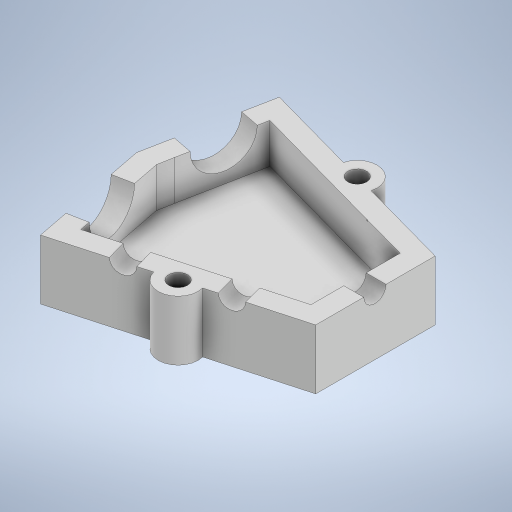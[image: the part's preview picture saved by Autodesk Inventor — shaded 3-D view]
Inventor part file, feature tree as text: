
AUTODESK INVENTOR PART (.ipt)
format: ipt  version: 2024 (Build 280153000, 153)  size: 374,272 bytes
history: native  units: in
note: dims shown in document units (in); Inventor stores cm internally (conversion verified against a paired STEP export)
features: extrude x8, sketch x8, mirror x2, projected_geometry x1
ambient origin geometry x8: Origin, YZ Plane, XZ Plane, XY Plane, X Axis, Y Axis, Z Axis, Center Point
bodies: Solid1 (feature_tree)
feature tree (19):
  extrude  "Extrusion1"  Depth=0.75in
  extrude  "Extrusion3"  Depth=0.75in
  extrude  "Extrusion4"  Depth=0.125in
  extrude  "Extrusion5"  Depth=0.375in TaperAngle=0.0deg
  extrude  "Extrusion6"  Depth=1.0in TaperAngle=0.0deg
  extrude  "Extrusion7"  Depth=1.0in TaperAngle=0.0deg
  extrude  "Extrusion8"  Depth=0.375in TaperAngle=0.0deg
  extrude  "Extrusion9"  Depth=0.375in TaperAngle=0.0deg
  mirror  "Mirror1"
  mirror  "Mirror2"
  sketch  "Sketch1"  dims[d0=1.0in d1=0.75in]
  sketch  "Sketch3"  dims[d2=0.5in d3=0.75in]
  sketch  "Sketch4"  dims[d4=0.125in d5=0.125in]
  sketch  "Sketch5"  dims[d6=0.125in d7=0.375in d8=0.0in]
  sketch  "Sketch6"  dims[d12=0.36in d13=1.0in d14=0.0in]
  projected_geometry  "Projected Loop1"
  sketch  "Sketch7"  dims[d15=0.36in d16=1.0in d17=0.0in]
  sketch  "Sketch8"  dims[d18=0.14in d19=0.375in d20=0.0in]
  sketch  "Sketch10"  dims[d21=0.125in d22=0.0in d23=0.375in d24=0.0in d25=0.1181in d26=0.1181in d27=0.375in d28=0.0in d29=0.14in d30=0.14in d31=0.15in d32=0.15in d33=0.375in d34=0.0in]
